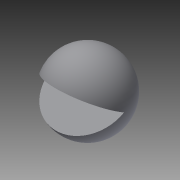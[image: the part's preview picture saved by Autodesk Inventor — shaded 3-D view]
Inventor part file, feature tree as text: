
AUTODESK INVENTOR PART (.ipt)
format: ipt  version: 2015 (Build 190159000, 159)  size: 107,520 bytes
history: native  units: in
note: dims shown in document units (in); Inventor stores cm internally (conversion verified against a paired STEP export)
features: sketch x2, revolve x1, extrude x1
ambient origin geometry x8: Origin, YZ Plane, XZ Plane, XY Plane, X Axis, Y Axis, Z Axis, Center Point
bodies: Solid1 (feature_tree)
feature tree (4):
  revolve  "Revolution1"  Angle=90.0deg
  extrude  "Extrusion1"  TaperAngle=30.0deg  [1 undecoded]
  sketch  "Sketch1"  dims[d0=1.1in d1=90.0deg]
  sketch  "Sketch3"  dims[d2=30.0deg d3=30.0deg d4=2.0in d5=0.0in]
note: 1 required parameter value undecoded (feature->parameter linkage not recoverable at this tier; creation-order binding heuristic only, values carry confidence <= 0.55)
